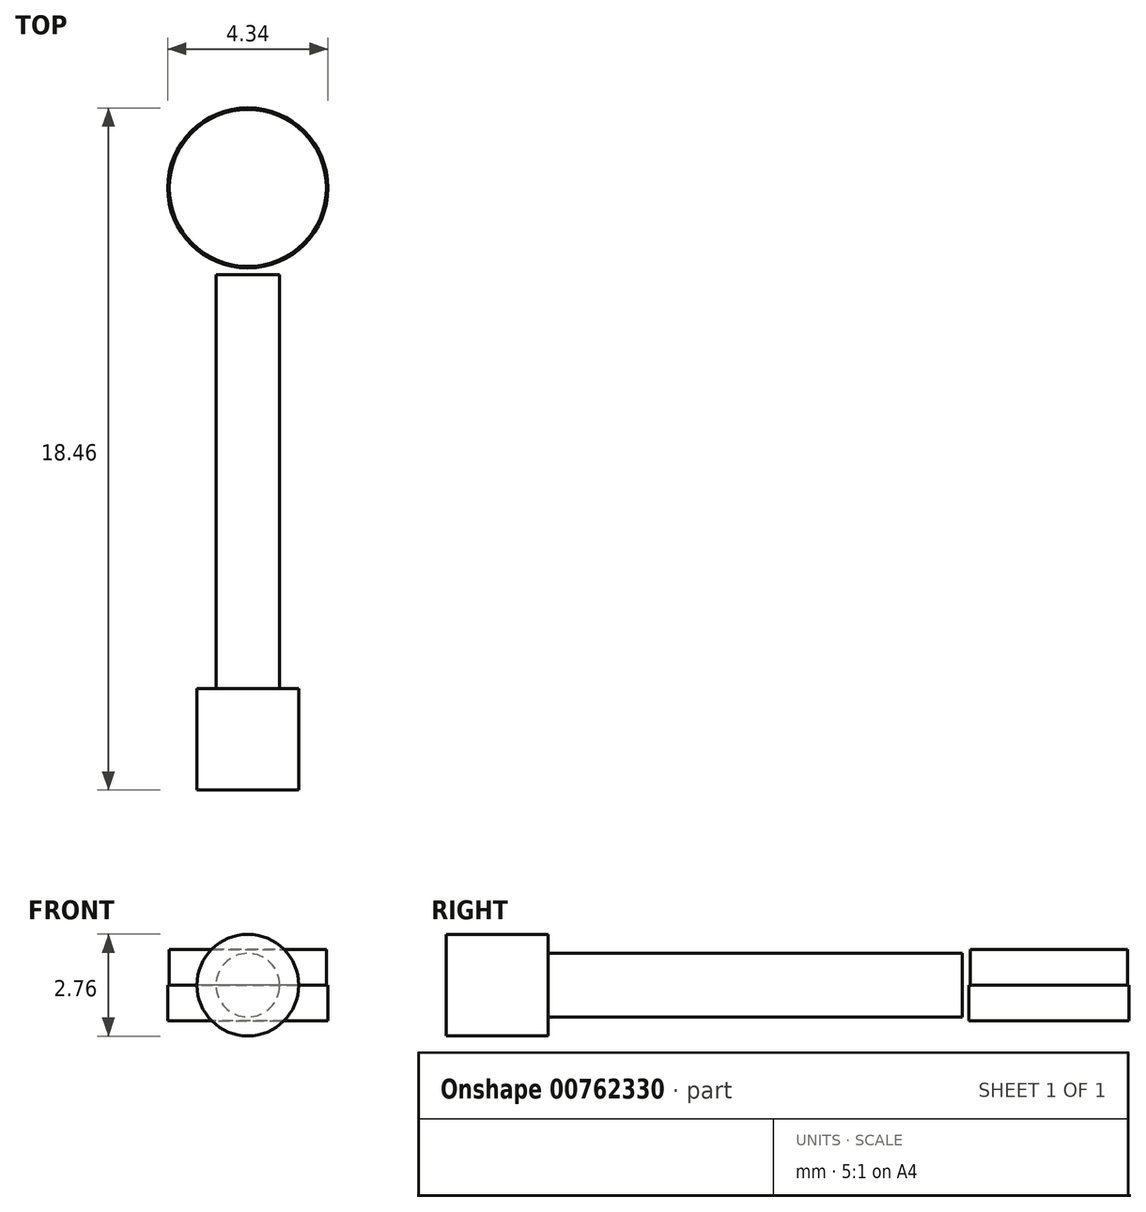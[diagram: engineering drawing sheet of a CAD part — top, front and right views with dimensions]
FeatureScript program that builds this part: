
annotation { "Feature Type Name" : "Feature", "Feature Type Description" : "" }
export const myFeature = defineFeature(function(context is Context, id is Id, definition is map)
    precondition{}
    {
        {
            var Q0;
            Q0=qCreatedBy(makeId("Front.planeOp"),FACE);
            var sketch = newSketch(context, id + "F0", { "sketchPlane" : qUnion([Q0])});
            skCircle(sketch, "E0", {"center": v(0, 0) * mm, "radius": 0.86 * mm});
            skSolve(sketch);
        }
        {
            var Q0;
            Q0 = qSketchRegion(id + "F0", true);
            extrude(context, id + "F1", {"entities" : qUnion([Q0]), "depth" : 11.2 * mm, "offsetDistance" : 25 * mm});
        }
        {
            var Q0;
            Q0=makeQuery(id+"F1.opExtrude","CAP_FACE",FACE,{"disambiguationData":[OSD([sQuery(id+"F0.wireOp",EDGE,"E0")])],"isStart":false});
            var sketch = newSketch(context, id + "F2", { "sketchPlane" : qUnion([Q0])});
            skCircle(sketch, "E1", {"center": v(0, 0) * mm, "radius": 1.38 * mm});
            skSolve(sketch);
        }
        {
            var Q0;
            Q0=makeQuery(id+"F2.imprint","IMPRINT",FACE,{"disambiguationData":[TD([[makeQuery(id+"F2.imprint","IMPRINT",EDGE,{"derivedFrom":sQuery(id+"F2.wireOp",EDGE,"E1")}),1.0]])]});
            var Q1;
            Q1=makeQuery(id+"F2.imprint","IMPRINT",FACE,{"disambiguationData":[TD([[makeQuery(id+"F2.imprint","IMPRINT",EDGE,{"derivedFrom":makeQuery(id+"F1.opExtrude","CAP_EDGE",EDGE,{"disambiguationData":[OSD([sQuery(id+"F0.wireOp",EDGE,"E0")])],"isStart":false})}),1.0]])]});
            var Q2;
            Q2=makeQuery(id+"F1.opExtrude","CAP_FACE",FACE,{"disambiguationData":[OSD([sQuery(id+"F0.wireOp",EDGE,"E0")])],"isStart":true});
            extrude(context, id + "F3", {"entities" : qUnion([Q0, Q1, Q2]), "operationType" : NewBodyOperationType.ADD, "depth" : 2.75 * mm, "offsetDistance" : 25 * mm});
        }
        {
            var Q0;
            Q0=qCreatedBy(makeId("Top.planeOp"),FACE);
            var sketch = newSketch(context, id + "F4", { "sketchPlane" : qUnion([Q0])});
            skLineSegment(sketch, "E2", {"start": v(0, 0) * mm, "end": v(0, 0.22) * mm});
            skCircle(sketch, "E3", {"center": v(0, 2.35) * mm, "radius": 2.12 * mm});
            skSolve(sketch);
        }
        {
            var Q0;
            Q0 = qSketchRegion(id + "F4", true);
            extrude(context, id + "F5", {"entities" : qUnion([Q0]), "depth" : .96 * mm, "offsetDistance" : 25 * mm});
        }
        {
            var Q0;
            Q0=makeQuery(id+"F5.opExtrude","CAP_FACE",FACE,{"disambiguationData":[OSD([sQuery(id+"F4.wireOp",EDGE,"E3")])],"isStart":true});
            var sketch = newSketch(context, id + "F6", { "sketchPlane" : qUnion([Q0])});
            skCircle(sketch, "E4", {"center": v(0, -2.35) * mm, "radius": 2.17 * mm});
            skSolve(sketch);
        }
        {
            var Q0;
            Q0 = qSketchRegion(id + "F6", true);
            extrude(context, id + "F7", {"entities" : qUnion([Q0]), "operationType" : NewBodyOperationType.ADD, "depth" : .96 * mm, "offsetDistance" : 25 * mm});
        }
    });
